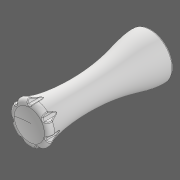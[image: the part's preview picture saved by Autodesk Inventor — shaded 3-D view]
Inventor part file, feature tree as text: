
AUTODESK INVENTOR PART (.ipt)
format: ipt  version: 2020 (Build 240168000, 168)  size: 566,272 bytes
history: native  units: in
note: dims shown in document units (in); Inventor stores cm internally (conversion verified against a paired STEP export)
features: fillet x2, sketch x2, revolve x1, extrude x1, pattern_circular x1
ambient origin geometry x8: Origin, YZ Plane, XZ Plane, XY Plane, X Axis, Y Axis, Z Axis, Center Point
bodies: Solid1 (feature_tree)
feature tree (7):
  revolve  "Revolution1"  [1 undecoded]
  extrude  "Extrusion1"  TaperAngle=90.0deg  [1 undecoded]
  pattern_circular  "Circular Pattern1"  [2 undecoded]
  fillet  "Fillet1"  Radius=0.2756in
  fillet  "Fillet3"  Radius=0.0984in
  sketch  "Sketch2"  dims[d1=0.2203in d4=0.0394in]
  sketch  "Sketch3"  dims[d6=1.1811in d7=90.0deg d10=0.0787in d11=0.2756in d12=0.0984in d13=0.6693in d14=0.0197in d15=0.1589in d16=45.0deg d17=45.0deg d18=0.0394in d19=0.1982in d24=0.3937in d25=0.0in d28=0.0197in d29=0.0098in d30=2.7559in d31=360.0deg]
note: 4 required parameter values undecoded (feature->parameter linkage not recoverable at this tier; creation-order binding heuristic only, values carry confidence <= 0.55)